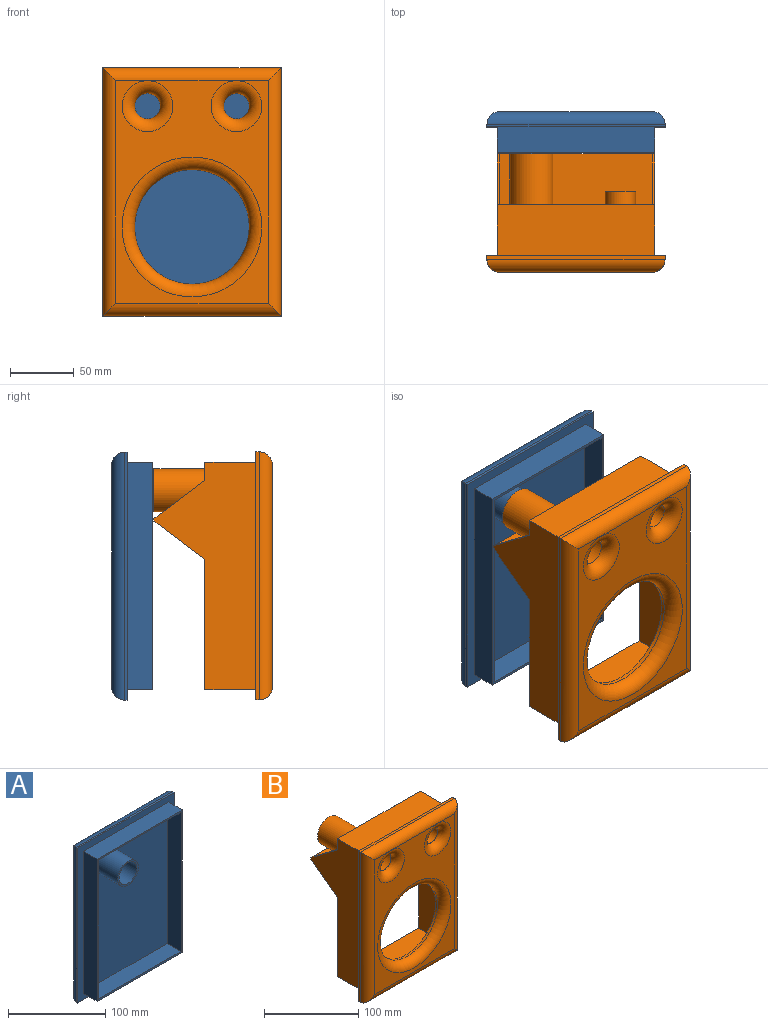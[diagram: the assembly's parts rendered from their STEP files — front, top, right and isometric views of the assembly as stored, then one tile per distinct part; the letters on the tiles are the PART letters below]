
ASSEMBLY  parts=2 mates=1
PART A: 26 faces, bbox 140x50x195 mm
  f0: plane 30x30mm, normal (0,-1,0), area 175.9mm2, adj f1,f2
  f1: cylinder r=13mm len=38mm, axis (0,1,0), area 3093.4mm2, adj f0,f3,f23,f24,f25
  f2: cylinder r=15mm len=38mm, axis (0,1,0), area 3571mm2, adj f0,f3,f23,f24,f25
  f3: plane 175x120mm, normal (0,-1,0), area 20831mm2, adj f1,f2,f7,f8,f9,f10,f24,f25
  f4: plane 179x20mm, normal (-1,0,0), area 3580mm2, adj f5,f11,f12,f22
  f5: plane 124x20mm, normal (0,0,-1), area 2480mm2, adj f4,f6,f12,f22
  f6: plane 179x20mm, normal (1,0,0), area 3580mm2, adj f5,f11,f12,f22
  f7: plane 120x20mm, normal (0,0,1), area 2400mm2, adj f3,f8,f10,f12
  f8: plane 175x20mm, normal (1,0,0), area 3500mm2, adj f3,f7,f9,f12
  f9: plane 120x20mm, normal (0,0,-1), area 2400mm2, adj f3,f8,f10,f12
  f10: plane 175x20mm, normal (-1,0,0), area 3500mm2, adj f3,f7,f9,f12
  f11: plane 124x20mm, normal (0,0,1), area 2480mm2, adj f4,f6,f12,f22
  f12: plane 179x124mm, normal (0,-1,0), area 1196mm2, adj f4,f5,f6,f7,f8,f9,f10,f11
  f13: plane 175x120mm, normal (0,1,0), area 21000mm2, adj f14,f15,f16,f17
  f14: cylinder r=10mm len=140mm, axis (1,0,0), area 2085mm2, adj f13,f15,f17,f18
  f15: cylinder r=10mm len=195mm, axis (0,0,-1), area 2948.9mm2, adj f13,f14,f16,f19
  f16: cylinder r=10mm len=140mm, axis (-1,0,0), area 2085mm2, adj f13,f15,f17,f20
  f17: cylinder r=10mm len=195mm, axis (0,0,1), area 2948.9mm2, adj f13,f14,f16,f21
  f18: plane 140x2mm, normal (0,0,-1), area 280mm2, adj f14,f19,f21,f22
  f19: plane 195x2mm, normal (-1,0,0), area 390mm2, adj f15,f18,f20,f22
  f20: plane 140x2mm, normal (0,0,1), area 280mm2, adj f16,f19,f21,f22
  f21: plane 195x2mm, normal (1,0,0), area 390mm2, adj f17,f18,f20,f22
  f22: plane 195x140mm, normal (0,-1,0), area 5104mm2, adj f4,f5,f6,f11,f18,f19,f20,f21
  f23: plane 3.47x2.14mm, normal (0,1,0), area 7mm2, adj f1,f2,f24,f25
  f24: plane 3x2.01mm, normal (-1,0,0), area 6mm2, adj f1,f2,f3,f23
  f25: plane 3x2.02mm, normal (1,0,0), area 6.1mm2, adj f1,f2,f3,f23
PART B: 75 faces, bbox 140x93x195 mm
  f0: plane 106.36x106.36mm, normal (0,1,0), area 3613.4mm2, adj f9,f42,f44,f46,f48,f58,f59,f60
  f1: plane 124x102.59mm, normal (0,1,0), area 650.4mm2, adj f26,f27,f29,f30,f32,f33,f38,f40
  f2: plane 120x42.41mm, normal (0,1,0), area 3728.7mm2, adj f3,f4,f22,f24,f31,f36
  f3: plane 80x42.41mm, normal (-1,0,0), area 2296.3mm2, adj f2,f31,f34,f36,f39
  f4: plane 80x42.41mm, normal (1,0,0), area 2296.3mm2, adj f2,f31,f34,f36,f41
  f5: plane 195x140mm, normal (0,1,0), area 5104mm2, adj f6,f7,f8,f12,f26,f27,f28,f33
  f6: plane 195x3mm, normal (1,0,0), area 585mm2, adj f5,f7,f12,f18
  f7: plane 140x3mm, normal (0,0,1), area 420mm2, adj f5,f6,f8,f20
  f8: plane 195x3mm, normal (-1,0,0), area 585mm2, adj f5,f7,f12,f21
  f9: cylinder r=45mm len=90mm, axis (0,1,0), area 848.2mm2, adj f0,f17
  f10: cylinder r=15.1mm len=83mm, axis (0,1,0), area 7874.7mm2, adj f13,f25
  f11: cylinder r=10mm len=53mm, axis (0,1,0), area 3330.1mm2, adj f15,f23
  f12: plane 140x3mm, normal (0,0,-1), area 420mm2, adj f5,f6,f8,f19
  f13: plane 30.2x30.2mm, normal (0,1,0), area 402.2mm2, adj f10,f16
  f14: plane 175x120mm, normal (0,-1,0), area 8983.4mm2, adj f15,f16,f17,f18,f19,f20,f21
  f15: torus R=20mm, axis (0,-1,0), area 1345.6mm2, adj f11,f14
  f16: torus R=20mm, axis (0,-1,0), area 1345.6mm2, adj f13,f14
  f17: torus R=55mm, axis (0,-1,0), area 4800mm2, adj f9,f14
  f18: cylinder r=10mm len=195mm, axis (0,0,-1), area 2948.9mm2, adj f6,f14,f19,f20
  f19: cylinder r=10mm len=140mm, axis (-1,0,0), area 2085mm2, adj f12,f14,f18,f21
  f20: cylinder r=10mm len=140mm, axis (1,0,0), area 2085mm2, adj f7,f14,f18,f21
  f21: cylinder r=10mm len=195mm, axis (0,0,1), area 2948.9mm2, adj f8,f14,f19,f20
  f22: cylinder r=12mm len=50mm, axis (0,-1,0), area 3769.9mm2, adj f2,f23
  f23: plane 24x24mm, normal (0,1,0), area 138.2mm2, adj f11,f22
  f24: cylinder r=17mm len=80mm, axis (0,-1,0), area 8545.1mm2, adj f2,f25
  f25: plane 34x34mm, normal (0,1,0), area 191.6mm2, adj f10,f24
  f26: plane 124x40mm, normal (0,0,-1), area 4960mm2, adj f1,f5,f27,f33
  f27: plane 179x80mm, normal (-1,0,0), area 8440mm2, adj f1,f5,f26,f28,f34,f37,f40,f41
  f28: plane 124x40mm, normal (0,0,1), area 4960mm2, adj f5,f27,f33,f34
  f29: plane 120x43.5mm, normal (0,0,1), area 5220mm2, adj f1,f30,f32,f74
  f30: plane 130.59x83.5mm, normal (-1,0,0), area 6280.7mm2, adj f1,f29,f35,f38,f74
  f31: plane 120x40mm, normal (0,0,-1), area 4800mm2, adj f2,f3,f4,f34
  f32: plane 130.59x83.5mm, normal (1,0,0), area 6280.7mm2, adj f1,f29,f35,f40,f74
  f33: plane 179x80mm, normal (1,0,0), area 8440mm2, adj f1,f5,f26,f28,f34,f37,f38,f39
  f34: plane 124x14.41mm, normal (0,1,0), area 297.6mm2, adj f3,f4,f27,f28,f31,f33,f39,f41
  f35: plane 120x83.5mm, normal (0,0,-1), area 10020mm2, adj f30,f32,f37,f74
  f36: plane 120x80mm, normal (0,0,1), area 9600mm2, adj f2,f3,f4,f37
  f37: plane 124x2mm, normal (0,1,0), area 248mm2, adj f27,f33,f35,f36,f38,f39,f40,f41
  f38: plane 40x30mm, normal (0,0.6,-0.8), area 100mm2, adj f1,f30,f33,f37
  f39: plane 40x30mm, normal (0,0.6,0.8), area 100mm2, adj f3,f33,f34,f37
  f40: plane 40x30mm, normal (0,0.6,-0.8), area 100mm2, adj f1,f27,f32,f37
  f41: plane 40x30mm, normal (0,0.6,0.8), area 100mm2, adj f4,f27,f34,f37
  f42: cylinder r=2.5mm len=5mm, axis (0,-1,0), area 47.1mm2, adj f0,f43
  f43: plane 5x5mm, normal (0,1,0), area 16.5mm2, adj f42,f52
  f44: cylinder r=2.5mm len=5mm, axis (0,-1,0), area 47.1mm2, adj f0,f45
  f45: plane 5x5mm, normal (0,1,0), area 16.5mm2, adj f44,f50
  f46: cylinder r=2.5mm len=5mm, axis (0,-1,0), area 47.1mm2, adj f0,f47
  f47: plane 5x5mm, normal (0,1,0), area 16.5mm2, adj f46,f56
  f48: cylinder r=2.5mm len=5mm, axis (0,-1,0), area 47.1mm2, adj f0,f49
  f49: plane 5x5mm, normal (0,1,0), area 16.5mm2, adj f48,f54
  f50: cylinder r=1mm len=10mm, axis (0,1,0), area 62.8mm2, adj f45,f51
  f51: cone r=0mm half-angle=59deg, axis (0,1,0), area 3.7mm2, adj f50
  f52: cylinder r=1mm len=10mm, axis (0,1,0), area 62.8mm2, adj f43,f53
  f53: cone r=0mm half-angle=59deg, axis (0,1,0), area 3.7mm2, adj f52
  f54: cylinder r=1mm len=10mm, axis (0,1,0), area 62.8mm2, adj f49,f55
  f55: cone r=0mm half-angle=59deg, axis (0,1,0), area 3.7mm2, adj f54
  f56: cylinder r=1mm len=10mm, axis (0,1,0), area 62.8mm2, adj f47,f57
  f57: cone r=0mm half-angle=59deg, axis (0,1,0), area 3.7mm2, adj f56
  f58: plane 7.07x7.07mm, normal (-0.71,0,-0.71), area 35mm2, adj f0,f59,f73,f74
  f59: cylinder r=53mm len=60.8mm, axis (0,1,0), area 226.6mm2, adj f0,f58,f60,f74
  f60: plane 7.07x7.07mm, normal (-0.71,0,0.71), area 35mm2, adj f0,f59,f61,f74
  f61: cylinder r=9.2mm len=15.71mm, axis (0,1,0), area 101.2mm2, adj f0,f60,f62,f74
  f62: plane 7.07x7.07mm, normal (0.71,0,-0.71), area 35mm2, adj f0,f61,f63,f74
  f63: cylinder r=53mm len=60.8mm, axis (0,1,0), area 226.6mm2, adj f0,f62,f64,f74
  f64: plane 7.07x7.07mm, normal (-0.71,0,-0.71), area 35mm2, adj f0,f63,f65,f74
  f65: cylinder r=9.2mm len=15.71mm, axis (0,1,0), area 101.2mm2, adj f0,f64,f66,f74
  f66: plane 7.07x7.07mm, normal (0.71,0,0.71), area 35mm2, adj f0,f65,f67,f74
  f67: cylinder r=53mm len=60.8mm, axis (0,1,0), area 226.6mm2, adj f0,f66,f68,f74
  f68: plane 7.07x7.07mm, normal (0.71,0,-0.71), area 35mm2, adj f0,f67,f69,f74
  f69: cylinder r=9.2mm len=15.71mm, axis (0,1,0), area 101.2mm2, adj f0,f68,f70,f74
  f70: plane 7.07x7.07mm, normal (-0.71,0,0.71), area 35mm2, adj f0,f69,f71,f74
  f71: cylinder r=53mm len=60.8mm, axis (0,1,0), area 226.6mm2, adj f0,f70,f72,f74
  f72: plane 7.07x7.07mm, normal (0.71,0,0.71), area 35mm2, adj f0,f71,f73,f74
  f73: cylinder r=9.2mm len=15.71mm, axis (0,1,0), area 101.2mm2, adj f0,f58,f72,f74
  f74: plane 130.59x120mm, normal (0,1,0), area 5617.4mm2, adj f29,f30,f32,f35,f58,f59,f60,f61
PLACE A t=(71.44,-44.15,-81.26)mm
PLACE B t=(131.88,-157.34,-171.15)mm
MATE slider B.f10 <-> A.f1  axis (0,-1,0) through (96.92,-77.34,-6.26)mm
